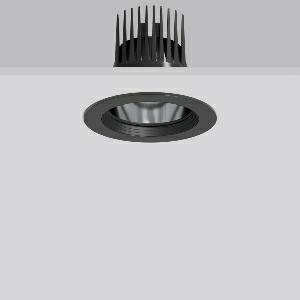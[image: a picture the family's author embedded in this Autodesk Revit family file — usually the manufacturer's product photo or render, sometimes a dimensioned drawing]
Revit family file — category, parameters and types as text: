
# Revit family: heledon_maxi_e_901764_003_76_6ebc
name_source: partatom
category: Lighting Fixtures
units: mm (PartAtom-declared; Revit-internal decimal feet)

## family parameters
Cut with Voids When Loaded = No
Host = Face
Light Source = No
Part Type = Normal
Room Calculation Point = No
Round Connector Dimension = Use Diameter
Shared = No

## types (1)
- HELEDON maxi E (1 x LED Modul 930, 4300 lm, 3000)
    Apparent Load = 35 VA
    Approval mark = CE
    CIE Flux Codes = 100 100 100 100 100
    Color Rendering = 90
    Color Temperature = 3000
    Default Elevation = 1800 mm
    Description = Series: HELEDON maxi
Round recessed downlight. Housing: die-cast aluminium, powder-coated. Black plastic ring and recessed LED to prevent glare from the side. Optical assembly with reflector made of MIRO-Silver with 98% total light reflection for outstanding efficiency - can be changed without tools. Best colour rendering index Ra>90. Suitable for Recessed ceiling mounting. Installation without tools thanks to spring fastening system. Including separate LED converter with connecting cable 600 mm.High quality converter without flickering and stroboscopic effect. Through-wiring box (5 pole) available as accessory. The following accessories can be mounted without use of tools: interchangeable lenses, decorative glasses, honeycomb louvre, clear and frosted diffusers, white interchangeable plastic ring. 
Colour: deep black, matt (RAL 9005)
Diameter: 162 mm
Height: 3 mm
Cut-out diameter: 152 mm
Recess height: 200 mm
Luminaire: recess height: 135 mm
Lamp: LED
Socket: without socket
Colour temperature: 3000K
Colour rendering index (CRI): 92
System power: 35 W
Rated luminous flux: 4300 lm
Luminous efficiency: 123 lm/W
Control gear: Converter, dimmable, DALI
Protection class: II
Type of protection: IP 20
    Height = 0 mm  [stored 0 ft]
    Lamp = 1 x LED Modul 930
    Lamp Light Flux = 4300 lm
    Lamp count = 1
    Length = 162 mm
    Lifetime = 50000 h
    Luminous efficacy = 123 lm/W
    Manufacturer = RZB
    ModVariant = No
    Model = 901764.003.76
    Mounting Place = Ceiling
    Mounting Type = Recessed
    Number of Poles = 1
    OnlyDefault = Yes
    Power Factor = 1
    Product Name = HELEDON maxi E
    Product group = Recessed downlights
    ProductGroupID = 402
    Protection Class = Protection class II
    Protection Degree = IP 20
    RLX_Detail_Level = 1
    RLX_Emergency_Light_Flux = 0 lm
    RLX_Emergency_Type = 0
    RLX_Emergency_Type_DB = No
    RlxData = <blob elided: 121349 chars, md5=8c7a3996>
    Socket = socket
    Standby Power = 0 W
    System Light Flux = 4300 lm
    System Power = 35 W
    Type Comments = Product without accessories
    Type Image = 901662.003.jpg
    URL = http://relux.com
    VarID = ---
    Voltage = 230 V
    Voltage Range = 220-240 V
    Weight = 0.00 kg
    Width = 0 mm  [stored 0 ft]

note: [stored X ft] marks values corroborated as IEEE doubles in the binary element streams (Revit-internal decimal feet)

## geometry (parser evidence)
native form markers: Blend x4, Sweep x13
no freeform markers — native parametric forms only
